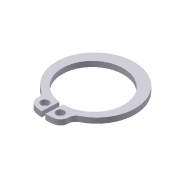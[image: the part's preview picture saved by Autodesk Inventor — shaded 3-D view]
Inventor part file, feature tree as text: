
AUTODESK INVENTOR PART (.ipt)
format: ipt  version: 2019 (Build 230136000, 136)  size: 230,912 bytes
history: native  units: mm (DEFAULTED — no unit token found)
features: other x2, plane x1
ambient origin geometry x8: Origin, YZ Plane, XZ Plane, XY Plane, X Axis, Y Axis, Z Axis, Center Point
bodies: Solid1 (feature_tree), Body (feature_tree)
feature tree (3):
  other  "JIS B 2804 12x1"
  other  "Work Axis1"
  plane  "Work Plane1"
